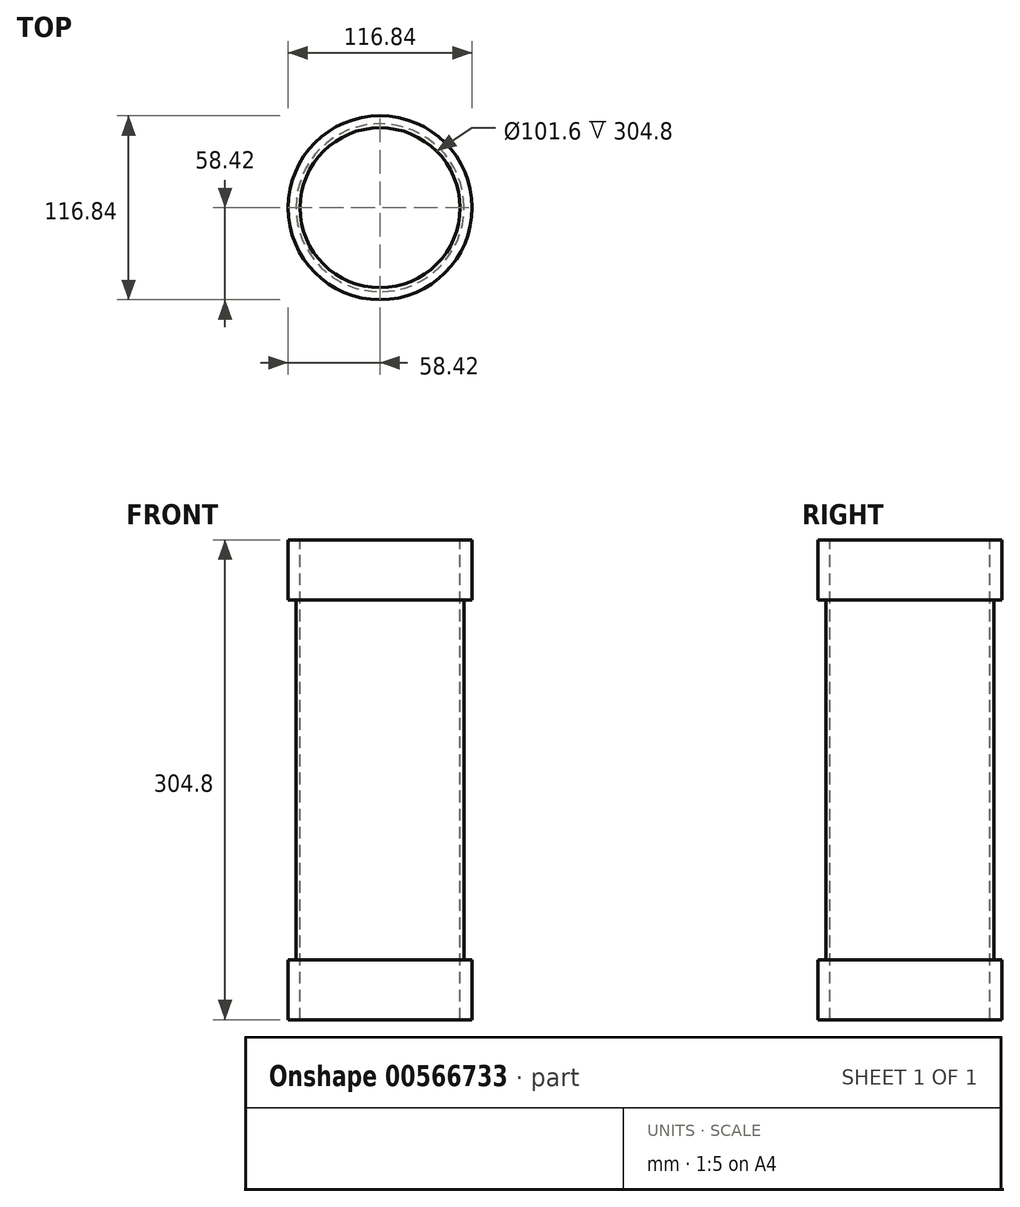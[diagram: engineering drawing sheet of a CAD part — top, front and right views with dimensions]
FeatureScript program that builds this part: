
annotation { "Feature Type Name" : "Feature", "Feature Type Description" : "" }
export const myFeature = defineFeature(function(context is Context, id is Id, definition is map)
    precondition{}
    {
        {
            var Q0;
            Q0=qCreatedBy(makeId("Top.planeOp"),FACE);
            var sketch = newSketch(context, id + "F0", { "sketchPlane" : qUnion([Q0])});
            skCircle(sketch, "E0", {"center": v(0, 0) * mm, "radius": 58.42 * mm});
            skSolve(sketch);
        }
        {
            var Q0;
            Q0=qCreatedBy(makeId("Top.planeOp"),FACE);
            var sketch = newSketch(context, id + "F1", { "sketchPlane" : qUnion([Q0])});
            skCircle(sketch, "E1", {"center": v(0, 0) * mm, "radius": 53.34 * mm});
            skSolve(sketch);
        }
        {
            var Q0;
            Q0=qCreatedBy(makeId("Top.planeOp"),FACE);
            var sketch = newSketch(context, id + "F2", { "sketchPlane" : qUnion([Q0])});
            skCircle(sketch, "E2", {"center": v(0, 0) * mm, "radius": 50.8 * mm});
            skSolve(sketch);
        }
        {
            var Q0;
            Q0 = qSketchRegion(id + "F0", true);
            extrude(context, id + "F3", {"entities" : qUnion([Q0]), "endBound" : BoundingType.SYMMETRIC, "depth" : 304.8 * mm, "offsetDistance" : 25.4 * mm});
        }
        {
            var Q0;
            Q0 = qSketchRegion(id + "F0", true);
            extrude(context, id + "F4", {"entities" : qUnion([Q0]), "operationType" : NewBodyOperationType.REMOVE, "endBound" : BoundingType.SYMMETRIC, "oppositeDirection" : true, "depth" : 228.6 * mm, "offsetDistance" : 25.4 * mm});
        }
        {
            var Q0;
            Q0 = qSketchRegion(id + "F1", true);
            extrude(context, id + "F5", {"entities" : qUnion([Q0]), "operationType" : NewBodyOperationType.ADD, "endBound" : BoundingType.SYMMETRIC, "depth" : 228.6 * mm, "offsetDistance" : 25.4 * mm});
        }
        {
            var Q0;
            Q0 = qSketchRegion(id + "F2", true);
            extrude(context, id + "F6", {"entities" : qUnion([Q0]), "operationType" : NewBodyOperationType.REMOVE, "endBound" : BoundingType.SYMMETRIC, "oppositeDirection" : true, "depth" : 304.8 * mm, "offsetDistance" : 25.4 * mm});
        }
    });
